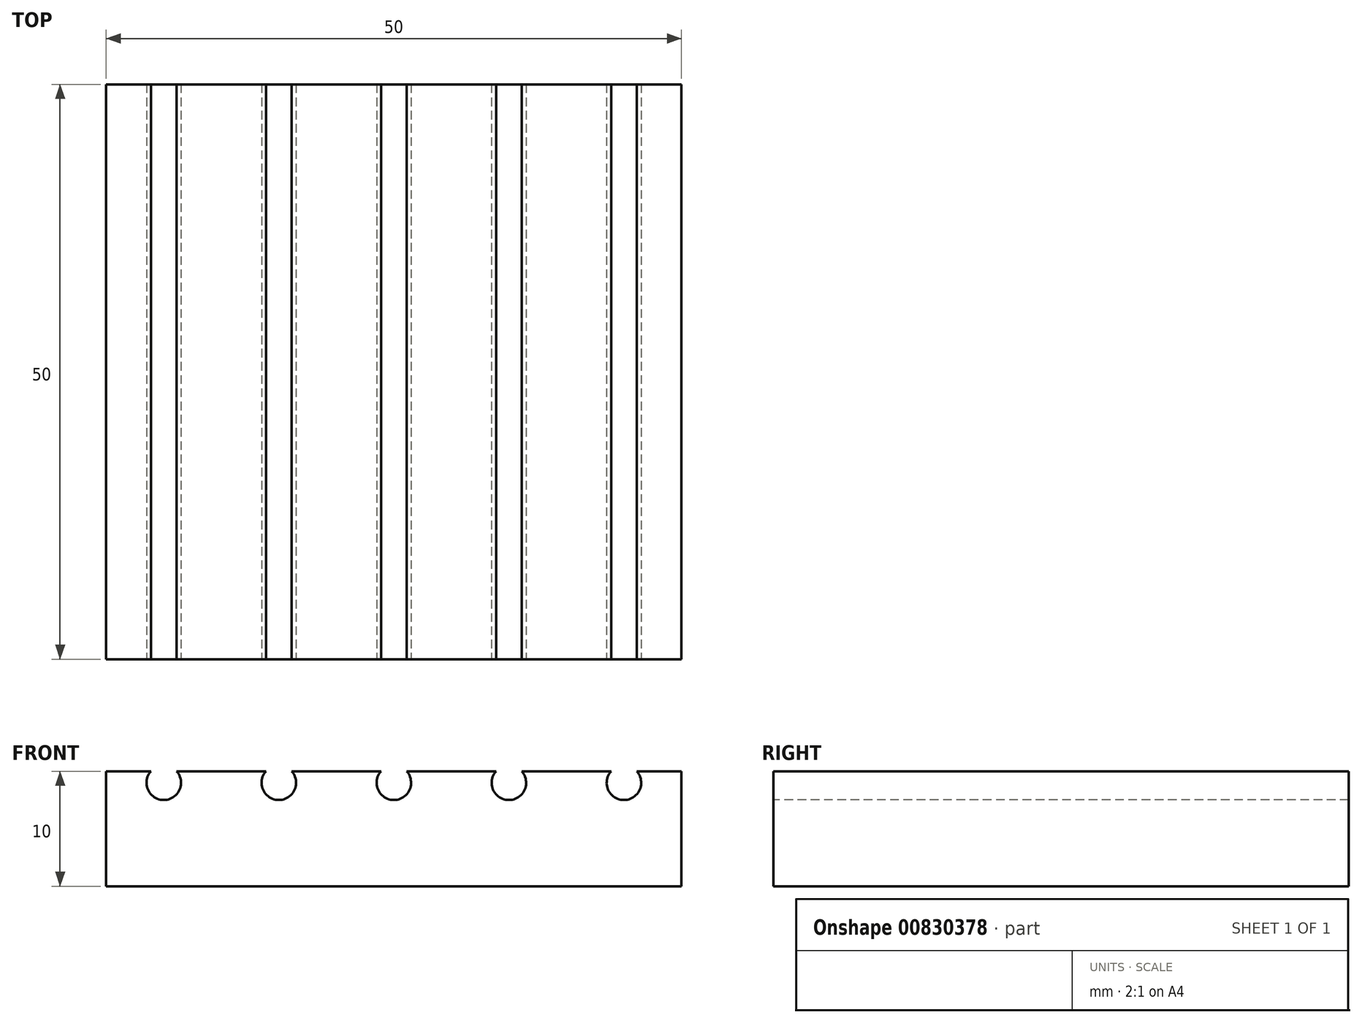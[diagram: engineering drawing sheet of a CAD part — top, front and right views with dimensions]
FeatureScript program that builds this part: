
annotation { "Feature Type Name" : "Feature", "Feature Type Description" : "" }
export const myFeature = defineFeature(function(context is Context, id is Id, definition is map)
    precondition{}
    {
        {
            var Q0;
            Q0=qCreatedBy(makeId("Top.planeOp"),FACE);
            var sketch = newSketch(context, id + "F0", { "sketchPlane" : qUnion([Q0])});
            skLineSegment(sketch, "E0.bottom", {"start": v(25, 25) * mm, "end": v(-25, 25) * mm});
            skLineSegment(sketch, "E0.top", {"start": v(25, -25) * mm, "end": v(-25, -25) * mm});
            skLineSegment(sketch, "E0.left", {"start": v(25, 25) * mm, "end": v(25, -25) * mm});
            skLineSegment(sketch, "E0.right", {"start": v(-25, 25) * mm, "end": v(-25, -25) * mm});
            skPoint(sketch, "E0.middle", {"position": v(0, 0) * mm});
            skSolve(sketch);
        }
        {
            var Q0;
            Q0=makeQuery(id+"F0.imprint","IMPRINT",FACE,{"disambiguationData":[TD([[makeQuery(id+"F0.imprint","IMPRINT",EDGE,{"derivedFrom":sQuery(id+"F0.wireOp",EDGE,"E0.bottom")}),1.0]])]});
            extrude(context, id + "F1", {"entities" : qUnion([Q0]), "depth" : 10 * mm, "offsetDistance" : 25 * mm});
        }
        {
            var Q0;
            Q0=makeQuery(id+"F1.opExtrude","SWEPT_FACE",FACE,{"disambiguationData":[OSD([sQuery(id+"F0.wireOp",EDGE,"E0.top")])]});
            var sketch = newSketch(context, id + "F2", { "sketchPlane" : qUnion([Q0])});
            skLineSegment(sketch, "E1.0.0", {"start": v(-25, 0) * mm, "end": v(25, 0) * mm});
            skLineSegment(sketch, "E1.0.1", {"start": v(25, 0) * mm, "end": v(25, 10) * mm});
            skLineSegment(sketch, "E1.0.2", {"start": v(25, 10) * mm, "end": v(-25, 10) * mm});
            skLineSegment(sketch, "E1.0.3", {"start": v(-25, 10) * mm, "end": v(-25, 0) * mm});
            skLineSegment(sketch, "E2", {"start": v(-25, 9) * mm, "end": v(25, 9) * mm, "construction": true});
            skCircle(sketch, "E3", {"center": v(-20, 9) * mm, "radius": 1.5 * mm});
            skCircle(sketch, "E4.1.0.0", {"center": v(-10, 9) * mm, "radius": 1.5 * mm});
            skCircle(sketch, "E4.2.0.0", {"center": v(0, 9) * mm, "radius": 1.5 * mm});
            skCircle(sketch, "E4.3.0.0", {"center": v(10, 9) * mm, "radius": 1.5 * mm});
            skLineSegment(sketch, "E4.direction1", {"start": v(-20, 9) * mm, "end": v(-10, 9) * mm, "construction": true});
            skLineSegment(sketch, "E5", {"start": v(0, 10) * mm, "end": v(0, 0) * mm, "construction": true});
            skCircle(sketch, "E6.0.4.0", {"center": v(20, 9) * mm, "radius": 1.5 * mm});
            skSolve(sketch);
        }
        {
            var Q0;
            {var subQ0=sQuery(id+"F2.wireOp",EDGE,"E4.5.0.0");var subQ1=sQuery(id+"F2.wireOp",EDGE,"E1.0.2");var subQ2=makeQuery(id+"F2.imprint","INTERSECT",VERTEX,{"disambiguationData":[OD(0.0)],"derivedFrom":[subQ1,subQ0]});Q0=makeQuery(id+"F2.imprint","IMPRINT",FACE,{"disambiguationData":[TD([[makeQuery(id+"F2.imprint","IMPRINT",EDGE,{"disambiguationData":[TD([[subQ2,-1.0]])],"derivedFrom":subQ1}),-1.0]])]});}
            var Q1;
            {var subQ0=sQuery(id+"F2.wireOp",EDGE,"E4.4.0.0");var subQ1=sQuery(id+"F2.wireOp",EDGE,"E1.0.2");var subQ2=makeQuery(id+"F2.imprint","INTERSECT",VERTEX,{"disambiguationData":[OD(0.0)],"derivedFrom":[subQ1,subQ0]});Q1=makeQuery(id+"F2.imprint","IMPRINT",FACE,{"disambiguationData":[TD([[makeQuery(id+"F2.imprint","IMPRINT",EDGE,{"disambiguationData":[TD([[subQ2,-1.0]])],"derivedFrom":subQ1}),-1.0]])]});}
            var Q2;
            {var subQ0=sQuery(id+"F2.wireOp",EDGE,"E4.3.0.0");var subQ1=sQuery(id+"F2.wireOp",EDGE,"E1.0.2");var subQ2=makeQuery(id+"F2.imprint","INTERSECT",VERTEX,{"disambiguationData":[OD(0.0)],"derivedFrom":[subQ1,subQ0]});Q2=makeQuery(id+"F2.imprint","IMPRINT",FACE,{"disambiguationData":[TD([[makeQuery(id+"F2.imprint","IMPRINT",EDGE,{"disambiguationData":[TD([[subQ2,-1.0]])],"derivedFrom":subQ1}),-1.0]])]});}
            var Q3;
            {var subQ0=sQuery(id+"F2.wireOp",EDGE,"E4.2.0.0");var subQ1=sQuery(id+"F2.wireOp",EDGE,"E1.0.2");var subQ2=makeQuery(id+"F2.imprint","INTERSECT",VERTEX,{"disambiguationData":[OD(0.0)],"derivedFrom":[subQ1,subQ0]});Q3=makeQuery(id+"F2.imprint","IMPRINT",FACE,{"disambiguationData":[TD([[makeQuery(id+"F2.imprint","IMPRINT",EDGE,{"disambiguationData":[TD([[subQ2,-1.0]])],"derivedFrom":subQ1}),-1.0]])]});}
            var Q4;
            {var subQ0=sQuery(id+"F2.wireOp",EDGE,"E4.1.0.0");var subQ1=sQuery(id+"F2.wireOp",EDGE,"E1.0.2");var subQ2=makeQuery(id+"F2.imprint","INTERSECT",VERTEX,{"disambiguationData":[OD(0.0)],"derivedFrom":[subQ1,subQ0]});Q4=makeQuery(id+"F2.imprint","IMPRINT",FACE,{"disambiguationData":[TD([[makeQuery(id+"F2.imprint","IMPRINT",EDGE,{"disambiguationData":[TD([[subQ2,-1.0]])],"derivedFrom":subQ1}),-1.0]])]});}
            var Q5;
            {var subQ0=sQuery(id+"F2.wireOp",EDGE,"E3");var subQ1=sQuery(id+"F2.wireOp",EDGE,"E1.0.2");var subQ2=makeQuery(id+"F2.imprint","INTERSECT",VERTEX,{"disambiguationData":[OD(0.0)],"derivedFrom":[subQ1,subQ0]});Q5=makeQuery(id+"F2.imprint","IMPRINT",FACE,{"disambiguationData":[TD([[makeQuery(id+"F2.imprint","IMPRINT",EDGE,{"disambiguationData":[TD([[subQ2,-1.0]])],"derivedFrom":subQ1}),-1.0]])]});}
            var Q6;
            {var subQ0=sQuery(id+"F2.wireOp",EDGE,"E4.5.0.0");var subQ1=sQuery(id+"F2.wireOp",EDGE,"E1.0.2");var subQ2=makeQuery(id+"F2.imprint","INTERSECT",VERTEX,{"disambiguationData":[OD(0.0)],"derivedFrom":[subQ1,subQ0]});Q6=makeQuery(id+"F2.imprint","IMPRINT",FACE,{"disambiguationData":[TD([[makeQuery(id+"F2.imprint","IMPRINT",EDGE,{"disambiguationData":[TD([[subQ2,-1.0]])],"derivedFrom":subQ1}),1.0]])]});}
            var Q7;
            {var subQ0=sQuery(id+"F2.wireOp",EDGE,"E4.4.0.0");var subQ1=sQuery(id+"F2.wireOp",EDGE,"E1.0.2");var subQ2=makeQuery(id+"F2.imprint","INTERSECT",VERTEX,{"disambiguationData":[OD(0.0)],"derivedFrom":[subQ1,subQ0]});Q7=makeQuery(id+"F2.imprint","IMPRINT",FACE,{"disambiguationData":[TD([[makeQuery(id+"F2.imprint","IMPRINT",EDGE,{"disambiguationData":[TD([[subQ2,-1.0]])],"derivedFrom":subQ1}),1.0]])]});}
            var Q8;
            {var subQ0=sQuery(id+"F2.wireOp",EDGE,"E4.3.0.0");var subQ1=sQuery(id+"F2.wireOp",EDGE,"E1.0.2");var subQ2=makeQuery(id+"F2.imprint","INTERSECT",VERTEX,{"disambiguationData":[OD(0.0)],"derivedFrom":[subQ1,subQ0]});Q8=makeQuery(id+"F2.imprint","IMPRINT",FACE,{"disambiguationData":[TD([[makeQuery(id+"F2.imprint","IMPRINT",EDGE,{"disambiguationData":[TD([[subQ2,-1.0]])],"derivedFrom":subQ1}),1.0]])]});}
            var Q9;
            {var subQ0=sQuery(id+"F2.wireOp",EDGE,"E4.2.0.0");var subQ1=sQuery(id+"F2.wireOp",EDGE,"E1.0.2");var subQ2=makeQuery(id+"F2.imprint","INTERSECT",VERTEX,{"disambiguationData":[OD(0.0)],"derivedFrom":[subQ1,subQ0]});Q9=makeQuery(id+"F2.imprint","IMPRINT",FACE,{"disambiguationData":[TD([[makeQuery(id+"F2.imprint","IMPRINT",EDGE,{"disambiguationData":[TD([[subQ2,-1.0]])],"derivedFrom":subQ1}),1.0]])]});}
            var Q10;
            {var subQ0=sQuery(id+"F2.wireOp",EDGE,"E4.1.0.0");var subQ1=sQuery(id+"F2.wireOp",EDGE,"E1.0.2");var subQ2=makeQuery(id+"F2.imprint","INTERSECT",VERTEX,{"disambiguationData":[OD(0.0)],"derivedFrom":[subQ1,subQ0]});Q10=makeQuery(id+"F2.imprint","IMPRINT",FACE,{"disambiguationData":[TD([[makeQuery(id+"F2.imprint","IMPRINT",EDGE,{"disambiguationData":[TD([[subQ2,-1.0]])],"derivedFrom":subQ1}),1.0]])]});}
            var Q11;
            {var subQ0=sQuery(id+"F2.wireOp",EDGE,"E3");var subQ1=sQuery(id+"F2.wireOp",EDGE,"E1.0.2");var subQ2=makeQuery(id+"F2.imprint","INTERSECT",VERTEX,{"disambiguationData":[OD(0.0)],"derivedFrom":[subQ1,subQ0]});Q11=makeQuery(id+"F2.imprint","IMPRINT",FACE,{"disambiguationData":[TD([[makeQuery(id+"F2.imprint","IMPRINT",EDGE,{"disambiguationData":[TD([[subQ2,-1.0]])],"derivedFrom":subQ1}),1.0]])]});}
            var Q12;
            {var subQ0=sQuery(id+"F2.wireOp",EDGE,"E6.0.4.0");var subQ1=sQuery(id+"F2.wireOp",EDGE,"E1.0.2");var subQ2=makeQuery(id+"F2.imprint","INTERSECT",VERTEX,{"disambiguationData":[OD(0.0)],"derivedFrom":[subQ1,subQ0]});Q12=makeQuery(id+"F2.imprint","IMPRINT",FACE,{"disambiguationData":[TD([[makeQuery(id+"F2.imprint","IMPRINT",EDGE,{"disambiguationData":[TD([[subQ2,-1.0]])],"derivedFrom":subQ1}),1.0]])]});}
            extrude(context, id + "F3", {"entities" : qUnion([Q0, Q1, Q2, Q3, Q4, Q5, Q6, Q7, Q8, Q9, Q10, Q11, Q12]), "operationType" : NewBodyOperationType.REMOVE, "endBound" : BoundingType.THROUGH_ALL, "oppositeDirection" : true, "depth" : 25 * mm, "offsetDistance" : 25 * mm});
        }
    });
